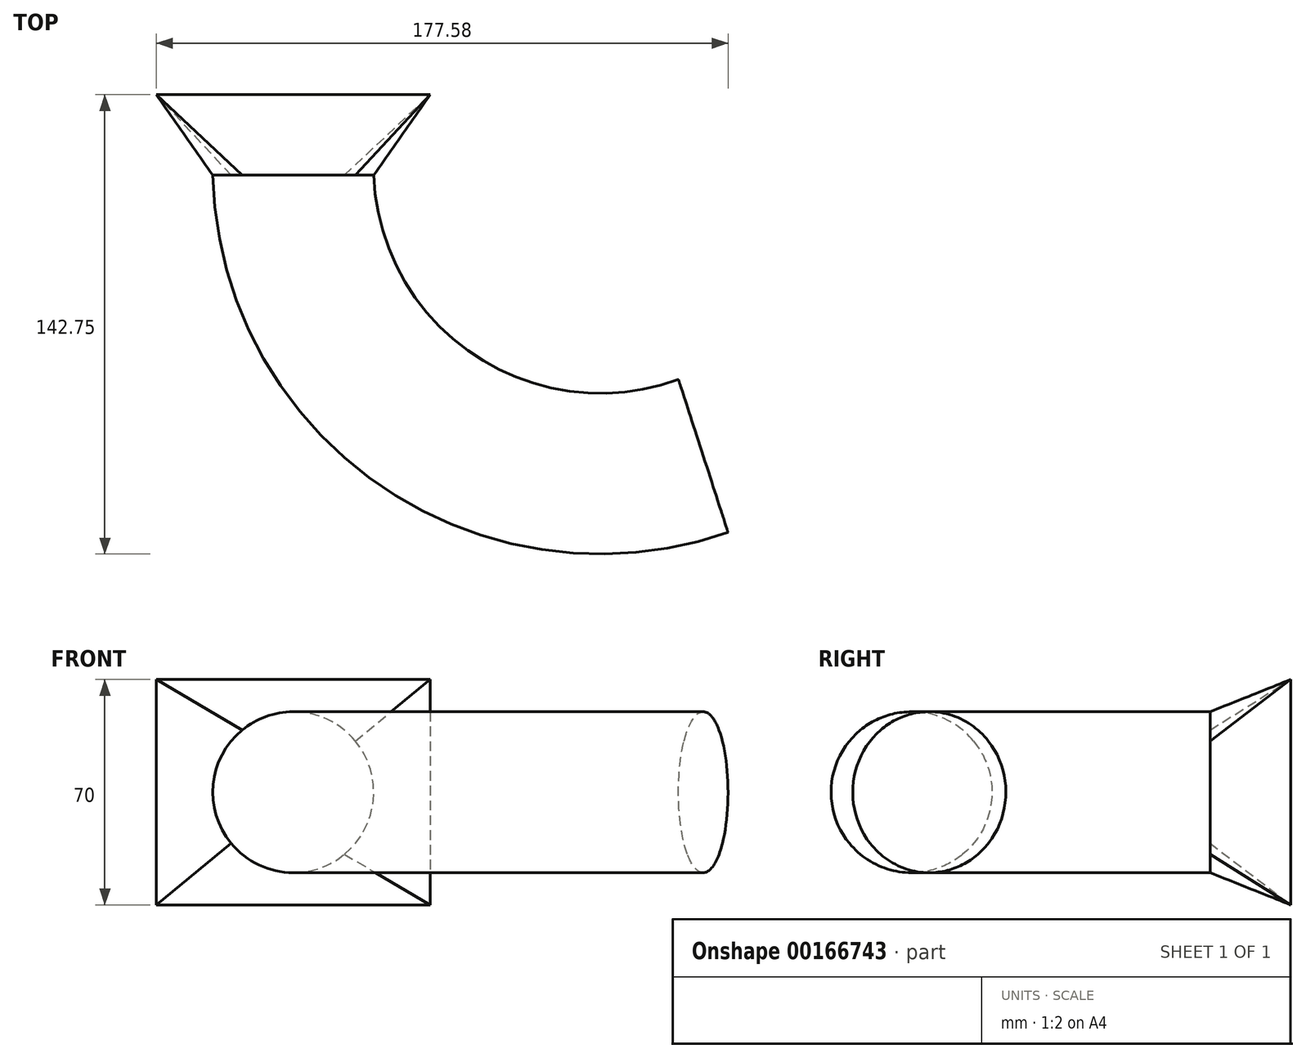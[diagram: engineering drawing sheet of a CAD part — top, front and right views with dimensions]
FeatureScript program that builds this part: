
annotation { "Feature Type Name" : "Feature", "Feature Type Description" : "" }
export const myFeature = defineFeature(function(context is Context, id is Id, definition is map)
    precondition{}
    {
        {
            var Q0;
            Q0=qCreatedBy(makeId("Front.planeOp"),FACE);
            cPlane(context, id + "F0", {"entities" : qUnion([Q0]), "cplaneType" : CPlaneType.OFFSET, "offset" : 25 * mm, "width" : 150 * mm, "height" : 150 * mm});
        }
        {
            var Q0;
            Q0=qCreatedBy(id+"F0.planeOp",FACE);
            var sketch = newSketch(context, id + "F1", { "sketchPlane" : qUnion([Q0])});
            skCircle(sketch, "E0", {"center": v(0, 0) * mm, "radius": 25 * mm});
            skSolve(sketch);
        }
        {
            var Q0;
            Q0=qCreatedBy(makeId("Front.planeOp"),FACE);
            var sketch = newSketch(context, id + "F2", { "sketchPlane" : qUnion([Q0])});
            skLineSegment(sketch, "E1.bottom", {"start": v(42.5, 35) * mm, "end": v(-42.5, 35) * mm});
            skLineSegment(sketch, "E1.top", {"start": v(42.5, -35) * mm, "end": v(-42.5, -35) * mm});
            skLineSegment(sketch, "E1.left", {"start": v(42.5, 35) * mm, "end": v(42.5, -35) * mm});
            skLineSegment(sketch, "E1.right", {"start": v(-42.5, 35) * mm, "end": v(-42.5, -35) * mm});
            skPoint(sketch, "E1.middle", {"position": v(0, 0) * mm});
            skSolve(sketch);
        }
        {
            var Q0;
            Q0 = qSketchRegion(id + "F1", true);
            var Q1;
            Q1 = qSketchRegion(id + "F2", true);
            loft(context, id + "F3", {"sheetProfilesArray" : [{ "sheetProfileEntities" : qUnion([Q0]) }, { "sheetProfileEntities" : qUnion([Q1]) }]});
        }
        {
            var Q0;
            Q0=qCreatedBy(makeId("Top.planeOp"),FACE);
            var sketch = newSketch(context, id + "F4", { "sketchPlane" : qUnion([Q0])});
            skArc(sketch, "E2", {"start": v(0, -25) * mm, "mid": v(41.47, -101.06) * mm, "end": v(127.37, -112.24) * mm});
            skSolve(sketch);
        }
        {
            var Q0;
            Q0=makeQuery(id+"F3.opLoft","CAP_FACE",FACE,{"disambiguationData":[OSD([makeQuery(id+"F1.imprint","IMPRINT",FACE,{"disambiguationData":[TD([[makeQuery(id+"F1.imprint","IMPRINT",EDGE,{"derivedFrom":sQuery(id+"F1.wireOp",EDGE,"E0")}),1.0]])]})])],"isStart":true});
            var Q1;
            Q1=sQuery(id+"F4.wireOp",EDGE,"E2");
            sweep(context, id + "F5", {"operationType" : NewBodyOperationType.ADD, "profiles" : qUnion([Q0]), "path" : qUnion([Q1])});
        }
    });
